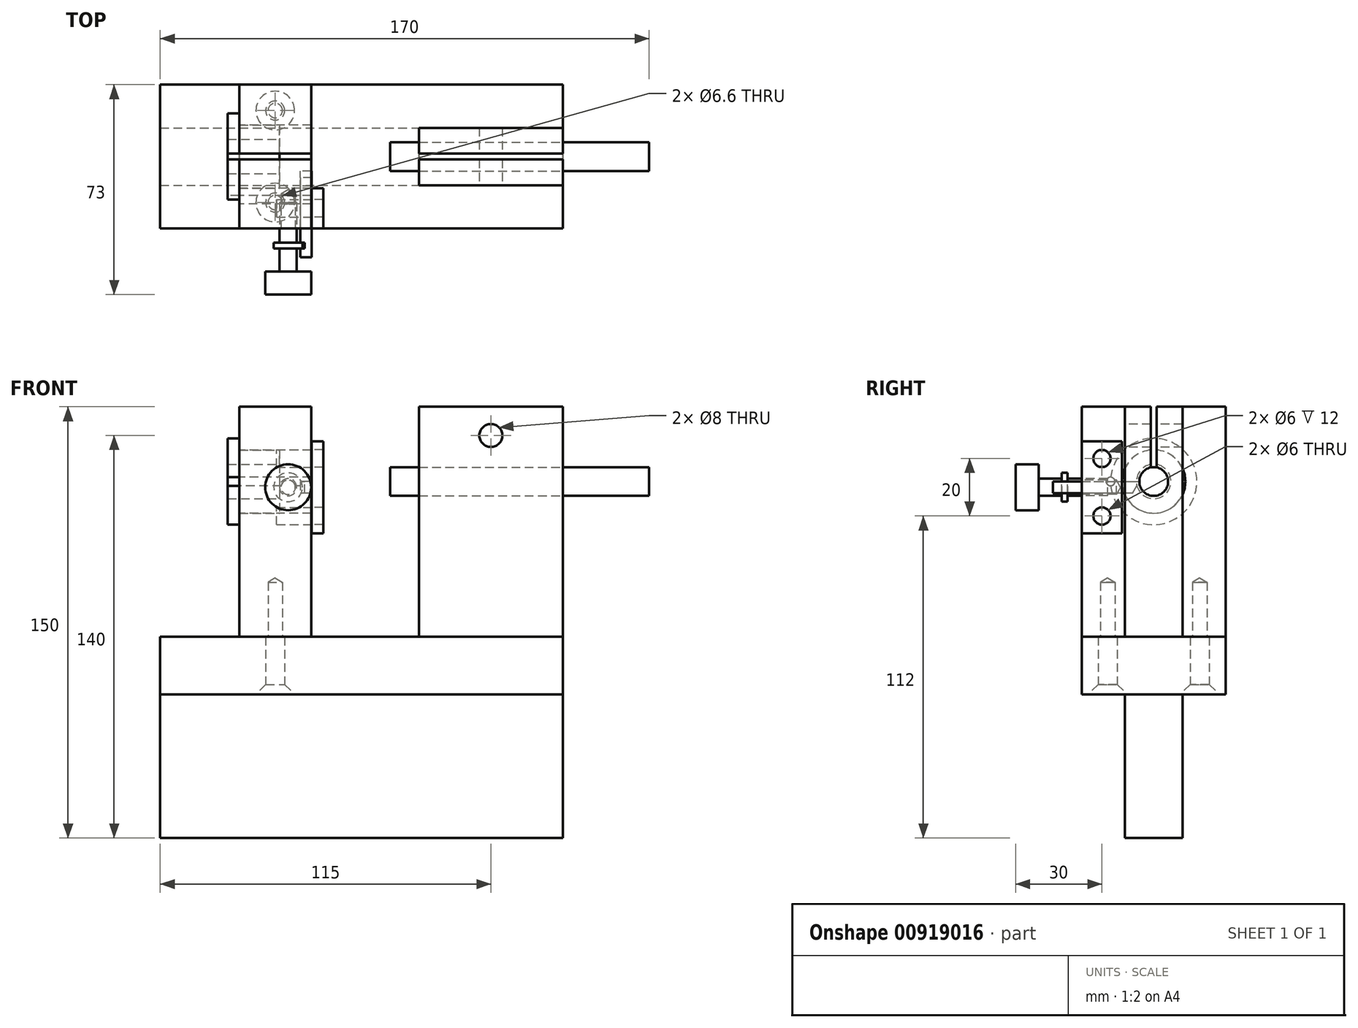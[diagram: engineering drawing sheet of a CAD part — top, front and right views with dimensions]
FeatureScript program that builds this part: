
annotation { "Feature Type Name" : "Feature", "Feature Type Description" : "" }
export const myFeature = defineFeature(function(context is Context, id is Id, definition is map)
    precondition{}
    {
        {
            var Q0;
            Q0=qCreatedBy(makeId("Right.planeOp"),FACE);
            var sketch = newSketch(context, id + "F0", { "sketchPlane" : qUnion([Q0])});
            skCircle(sketch, "E0", {"center": v(0, 0) * mm, "radius": 11 * mm});
            skLineSegment(sketch, "E1.bottom", {"start": v(25, 26) * mm, "end": v(-25, 26) * mm});
            skLineSegment(sketch, "E1.top", {"start": v(25, -54) * mm, "end": v(-25, -54) * mm});
            skLineSegment(sketch, "E1.left", {"start": v(25, 26) * mm, "end": v(25, -54) * mm});
            skLineSegment(sketch, "E1.right", {"start": v(-25, 26) * mm, "end": v(-25, -54) * mm});
            skSolve(sketch);
        }
        {
            var Q0;
            Q0 = qSketchRegion(id + "F0", true);
            extrude(context, id + "F1", {"entities" : qUnion([Q0]), "depth" : 12.5 * mm, "offsetDistance" : 25 * mm, "hasSecondDirection" : true, "secondDirectionOppositeDirection" : true, "secondDirectionDepth" : 12.5 * mm});
        }
        {
            var Q0;
            Q0=makeQuery(id+"F1.opExtrude","CAP_FACE",FACE,{"disambiguationData":[OSD([sQuery(id+"F0.wireOp",EDGE,"E0"),sQuery(id+"F0.wireOp",EDGE,"E1.bottom"),sQuery(id+"F0.wireOp",EDGE,"E1.top"),sQuery(id+"F0.wireOp",EDGE,"E1.left"),sQuery(id+"F0.wireOp",EDGE,"E1.right")])],"isStart":true});
            var sketch = newSketch(context, id + "F2", { "sketchPlane" : qUnion([Q0])});
            skCircle(sketch, "E2", {"center": v(15, 0) * mm, "radius": 1.5 * mm});
            skSolve(sketch);
        }
        {
            var Q0;
            Q0 = qSketchRegion(id + "F2", true);
            extrude(context, id + "F3", {"entities" : qUnion([Q0]), "operationType" : NewBodyOperationType.REMOVE, "oppositeDirection" : true, "depth" : 10 * mm, "offsetDistance" : 25 * mm});
        }
        {
            var Q0;
            Q0=makeQuery(id+"F1.opExtrude","SWEPT_FACE",FACE,{"disambiguationData":[OSD([sQuery(id+"F0.wireOp",EDGE,"E1.top")])]});
            var sketch = newSketch(context, id + "F4", { "sketchPlane" : qUnion([Q0])});
            skLineSegment(sketch, "E3.bottom", {"start": v(100, -25) * mm, "end": v(-40, -25) * mm});
            skLineSegment(sketch, "E3.top", {"start": v(100, 25) * mm, "end": v(-40, 25) * mm});
            skLineSegment(sketch, "E3.left", {"start": v(100, -25) * mm, "end": v(100, 25) * mm});
            skLineSegment(sketch, "E3.right", {"start": v(-40, -25) * mm, "end": v(-40, 25) * mm});
            skPoint(sketch, "E3.middle", {"position": v(0, 0) * mm});
            skSolve(sketch);
        }
        {
            var Q0;
            Q0 = qSketchRegion(id + "F4", true);
            extrude(context, id + "F5", {"entities" : qUnion([Q0]), "depth" : 20 * mm, "offsetDistance" : 25 * mm});
        }
        {
            var Q0;
            Q0=makeQuery(id+"F1.opExtrude","CAP_FACE",FACE,{"disambiguationData":[OSD([sQuery(id+"F0.wireOp",EDGE,"E0"),sQuery(id+"F0.wireOp",EDGE,"E1.bottom"),sQuery(id+"F0.wireOp",EDGE,"E1.top"),sQuery(id+"F0.wireOp",EDGE,"E1.left"),sQuery(id+"F0.wireOp",EDGE,"E1.right")])],"isStart":false});
            var sketch = newSketch(context, id + "F6", { "sketchPlane" : qUnion([Q0])});
            skLineSegment(sketch, "E4.bottom", {"start": v(6, 6) * mm, "end": v(-6, 6) * mm});
            skLineSegment(sketch, "E4.top", {"start": v(6, -6) * mm, "end": v(-6, -6) * mm});
            skLineSegment(sketch, "E4.left", {"start": v(6, 6) * mm, "end": v(6, -6) * mm});
            skLineSegment(sketch, "E4.right", {"start": v(-6, 6) * mm, "end": v(-6, -6) * mm});
            skPoint(sketch, "E4.middle", {"position": v(0, 0) * mm});
            skCircle(sketch, "E5", {"center": v(0, 0) * mm, "radius": 8.49 * mm});
            skCircle(sketch, "E6", {"center": v(0, 0) * mm, "radius": 6 * mm});
            skSolve(sketch);
        }
        {
            var Q0;
            Q0=qCreatedBy(makeId("Front.planeOp"),FACE);
            var sketch = newSketch(context, id + "F7", { "sketchPlane" : qUnion([Q0])});
            skLineSegment(sketch, "E7", {"start": v(16.61, 0) * mm, "end": v(-49.8, 0) * mm, "construction": true});
            skLineSegment(sketch, "E8", {"start": v(1.5, 6) * mm, "end": v(1.5, 11) * mm});
            skLineSegment(sketch, "E9", {"start": v(1.5, 11) * mm, "end": v(-12.5, 11) * mm});
            skLineSegment(sketch, "E10", {"start": v(-12.5, 11) * mm, "end": v(-12.5, 15) * mm});
            skLineSegment(sketch, "E11", {"start": v(-12.5, 15) * mm, "end": v(-16.5, 15) * mm});
            skLineSegment(sketch, "E12", {"start": v(-16.5, 15) * mm, "end": v(-16.5, 6) * mm});
            skLineSegment(sketch, "E13", {"start": v(-16.5, 6) * mm, "end": v(1.5, 6) * mm});
            skSolve(sketch);
        }
        {
            var Q0;
            Q0 = qSketchRegion(id + "F7", true);
            var Q1;
            Q1=sQuery(id+"F7.wireOp",EDGE,"E7");
            revolve(context, id + "F8", {"surfaceOperationType" : NewSurfaceOperationType.NEW, "entities" : qUnion([Q0]), "axis" : qUnion([Q1]), "revolveType" : RevolveType.FULL});
        }
        {
            var Q0;
            Q0=makeQuery(id+"F8.opRevolve","SWEPT_FACE",FACE,{"disambiguationData":[OSD([sQuery(id+"F7.wireOp",EDGE,"E12")])]});
            var sketch = newSketch(context, id + "F9", { "sketchPlane" : qUnion([Q0])});
            skCircle(sketch, "E14", {"center": v(15, 0) * mm, "radius": 1.5 * mm});
            skSolve(sketch);
        }
        {
            var Q0;
            Q0 = qSketchRegion(id + "F9", true);
            extrude(context, id + "F10", {"entities" : qUnion([Q0]), "operationType" : NewBodyOperationType.REMOVE, "endBound" : BoundingType.THROUGH_ALL, "oppositeDirection" : true, "depth" : 25 * mm, "offsetDistance" : 25 * mm});
        }
        {
            var Q0;
            Q0=makeQuery(id+"F6.imprint","IMPRINT",FACE,{"disambiguationData":[TD([[makeQuery(id+"F6.imprint","IMPRINT",EDGE,{"derivedFrom":makeQuery(id+"F1.opExtrude","CAP_EDGE",EDGE,{"disambiguationData":[OSD([sQuery(id+"F0.wireOp",EDGE,"E0")])],"isStart":false})}),-1.0]])]});
            var sketch = newSketch(context, id + "F11", { "sketchPlane" : qUnion([Q0])});
            skLineSegment(sketch, "E15", {"start": v(-36.13, 0) * mm, "end": v(-7.22, 0) * mm});
            skLineSegment(sketch, "E16", {"start": v(-7.22, 0) * mm, "end": v(-10, -4) * mm});
            skLineSegment(sketch, "E17", {"start": v(-10, -4) * mm, "end": v(-36.13, -4) * mm});
            skLineSegment(sketch, "E18", {"start": v(-36.13, -4) * mm, "end": v(-36.13, 0) * mm});
            skSolve(sketch);
        }
        {
            var Q0;
            Q0 = qSketchRegion(id + "F11", true);
            extrude(context, id + "F12", {"entities" : qUnion([Q0]), "operationType" : NewBodyOperationType.REMOVE, "oppositeDirection" : true, "depth" : 3.8 * mm, "offsetDistance" : 25 * mm});
        }
        {
            var Q0;
            Q0=makeQuery(id+"F12.boolean.opBoolean","COPY",FACE,{"derivedFrom":makeQuery(id+"F12.opExtrude","CAP_FACE",FACE,{"disambiguationData":[OSD([sQuery(id+"F11.wireOp",EDGE,"E15"),sQuery(id+"F11.wireOp",EDGE,"E16"),sQuery(id+"F11.wireOp",EDGE,"E17"),sQuery(id+"F11.wireOp",EDGE,"E18")])],"isStart":false})});
            var sketch = newSketch(context, id + "F13", { "sketchPlane" : qUnion([Q0])});
            skLineSegment(sketch, "E19.0", {"start": v(-35, 0) * mm, "end": v(-5, 0) * mm});
            skLineSegment(sketch, "E20.0", {"start": v(-7.3, -4) * mm, "end": v(-35, -4) * mm});
            skLineSegment(sketch, "E21", {"start": v(-7.3, -4) * mm, "end": v(-5, 0) * mm});
            skLineSegment(sketch, "E22", {"start": v(0, 0) * mm, "end": v(0, 13.61) * mm, "construction": true});
            skLineSegment(sketch, "E23", {"start": v(-35, 0) * mm, "end": v(-35, -4) * mm});
            skPoint(sketch, "E24.orphan", {"position": v(-25, 0) * mm});
            skPoint(sketch, "E25.orphan", {"position": v(-25, -4) * mm});
            skPoint(sketch, "E26.orphan", {"position": v(-11, 0) * mm});
            skPoint(sketch, "E27.orphan", {"position": v(-10.25, -4) * mm});
            skSolve(sketch);
        }
        {
            var Q0;
            Q0 = qSketchRegion(id + "F13", true);
            extrude(context, id + "F14", {"entities" : qUnion([Q0]), "depth" : 4 * mm, "offsetDistance" : 25 * mm});
        }
        {
            var Q0;
            Q0=makeQuery(id+"F6.imprint","IMPRINT",FACE,{"disambiguationData":[TD([[makeQuery(id+"F6.imprint","IMPRINT",EDGE,{"derivedFrom":makeQuery(id+"F1.opExtrude","CAP_EDGE",EDGE,{"disambiguationData":[OSD([sQuery(id+"F0.wireOp",EDGE,"E0")])],"isStart":false})}),-1.0]])]});
            var sketch = newSketch(context, id + "F15", { "sketchPlane" : qUnion([Q0])});
            skCircle(sketch, "E28", {"center": v(-18, 8) * mm, "radius": 3 * mm});
            skCircle(sketch, "E29", {"center": v(-18, -12) * mm, "radius": 3 * mm});
            skSolve(sketch);
        }
        {
            var Q0;
            Q0 = qSketchRegion(id + "F15", true);
            extrude(context, id + "F16", {"entities" : qUnion([Q0]), "operationType" : NewBodyOperationType.REMOVE, "oppositeDirection" : true, "depth" : 12 * mm, "offsetDistance" : 25 * mm});
        }
        {
            var Q0;
            Q0=makeQuery(id+"F14.opExtrude","SWEPT_FACE",FACE,{"disambiguationData":[OSD([sQuery(id+"F13.wireOp",EDGE,"E19.0")])]});
            var sketch = newSketch(context, id + "F17", { "sketchPlane" : qUnion([Q0])});
            skLineSegment(sketch, "E30.bottom", {"start": v(8.7, -32) * mm, "end": v(10.2, -32) * mm});
            skLineSegment(sketch, "E30.top", {"start": v(8.7, -30) * mm, "end": v(10.2, -30) * mm});
            skLineSegment(sketch, "E30.left", {"start": v(8.7, -32) * mm, "end": v(8.7, -30) * mm});
            skLineSegment(sketch, "E30.right", {"start": v(10.2, -32) * mm, "end": v(10.2, -30) * mm});
            skSolve(sketch);
        }
        {
            var Q0;
            Q0 = qSketchRegion(id + "F17", true);
            extrude(context, id + "F18", {"entities" : qUnion([Q0]), "operationType" : NewBodyOperationType.REMOVE, "endBound" : BoundingType.THROUGH_ALL, "oppositeDirection" : true, "depth" : 25 * mm, "offsetDistance" : 25 * mm});
        }
        {
            var Q0;
            Q0=makeQuery(id+"F5.opExtrude","CAP_FACE",FACE,{"disambiguationData":[OSD([sQuery(id+"F4.wireOp",EDGE,"E3.bottom"),sQuery(id+"F4.wireOp",EDGE,"E3.top"),sQuery(id+"F4.wireOp",EDGE,"E3.left"),sQuery(id+"F4.wireOp",EDGE,"E3.right")])],"isStart":true});
            var sketch = newSketch(context, id + "F19", { "sketchPlane" : qUnion([Q0])});
            skLineSegment(sketch, "E31.bottom", {"start": v(100, -10) * mm, "end": v(50, -10) * mm});
            skLineSegment(sketch, "E31.top", {"start": v(100, 10) * mm, "end": v(50, 10) * mm});
            skLineSegment(sketch, "E31.left", {"start": v(100, -10) * mm, "end": v(100, 10) * mm});
            skLineSegment(sketch, "E31.right", {"start": v(50, -10) * mm, "end": v(50, 10) * mm});
            skSolve(sketch);
        }
        {
            var Q0;
            Q0 = qSketchRegion(id + "F19", true);
            extrude(context, id + "F20", {"entities" : qUnion([Q0]), "depth" : 80 * mm, "offsetDistance" : 25 * mm});
        }
        {
            var Q0;
            Q0=makeQuery(id+"F20.opExtrude","SWEPT_FACE",FACE,{"disambiguationData":[OSD([sQuery(id+"F19.wireOp",EDGE,"E31.left")])]});
            var sketch = newSketch(context, id + "F21", { "sketchPlane" : qUnion([Q0])});
            skCircle(sketch, "E32", {"center": v(0, 0) * mm, "radius": 5 * mm});
            skSolve(sketch);
        }
        {
            var Q0;
            Q0 = qSketchRegion(id + "F21", true);
            extrude(context, id + "F22", {"entities" : qUnion([Q0]), "operationType" : NewBodyOperationType.REMOVE, "endBound" : BoundingType.THROUGH_ALL, "oppositeDirection" : true, "depth" : 25 * mm, "offsetDistance" : 25 * mm});
        }
        {
            var Q0;
            Q0=makeQuery(id+"F20.opExtrude","SWEPT_FACE",FACE,{"disambiguationData":[OSD([sQuery(id+"F19.wireOp",EDGE,"E31.left")])]});
            var sketch = newSketch(context, id + "F23", { "sketchPlane" : qUnion([Q0])});
            skLineSegment(sketch, "E33.bottom", {"start": v(-1, 0) * mm, "end": v(1, 0) * mm});
            skLineSegment(sketch, "E33.top", {"start": v(-1, 26) * mm, "end": v(1, 26) * mm});
            skLineSegment(sketch, "E33.left", {"start": v(-1, 0) * mm, "end": v(-1, 26) * mm});
            skLineSegment(sketch, "E33.right", {"start": v(1, 0) * mm, "end": v(1, 26) * mm});
            skSolve(sketch);
        }
        {
            var Q0;
            Q0 = qSketchRegion(id + "F23", true);
            extrude(context, id + "F24", {"entities" : qUnion([Q0]), "operationType" : NewBodyOperationType.REMOVE, "endBound" : BoundingType.THROUGH_ALL, "oppositeDirection" : true, "depth" : 25 * mm, "offsetDistance" : 25 * mm});
        }
        {
            var Q0;
            Q0=makeQuery(id+"F20.opExtrude","SWEPT_FACE",FACE,{"disambiguationData":[OSD([sQuery(id+"F19.wireOp",EDGE,"E31.bottom")])]});
            var sketch = newSketch(context, id + "F25", { "sketchPlane" : qUnion([Q0])});
            skCircle(sketch, "E34", {"center": v(75, 16) * mm, "radius": 4 * mm});
            skPoint(sketch, "E34.centerSnap0", {"position": v(75, 26) * mm});
            skSolve(sketch);
        }
        {
            var Q0;
            Q0 = qSketchRegion(id + "F25", true);
            extrude(context, id + "F26", {"entities" : qUnion([Q0]), "operationType" : NewBodyOperationType.REMOVE, "endBound" : BoundingType.THROUGH_ALL, "oppositeDirection" : true, "depth" : 25 * mm, "offsetDistance" : 25 * mm});
        }
        {
            var Q0;
            Q0=makeQuery(id+"F20.opExtrude","SWEPT_FACE",FACE,{"disambiguationData":[OSD([sQuery(id+"F19.wireOp",EDGE,"E31.right")])]});
            var sketch = newSketch(context, id + "F27", { "sketchPlane" : qUnion([Q0])});
            skCircle(sketch, "E35", {"center": v(0, 0) * mm, "radius": 5 * mm});
            skSolve(sketch);
        }
        {
            var Q0;
            Q0 = qSketchRegion(id + "F27", true);
            extrude(context, id + "F28", {"entities" : qUnion([Q0]), "depth" : 10 * mm, "offsetDistance" : 25 * mm, "hasSecondDirection" : true, "secondDirectionOppositeDirection" : true, "secondDirectionDepth" : 80 * mm});
        }
        {
            var Q0;
            Q0=makeQuery(id+"F5.opExtrude","CAP_FACE",FACE,{"disambiguationData":[OSD([sQuery(id+"F4.wireOp",EDGE,"E3.bottom"),sQuery(id+"F4.wireOp",EDGE,"E3.top"),sQuery(id+"F4.wireOp",EDGE,"E3.left"),sQuery(id+"F4.wireOp",EDGE,"E3.right")])],"isStart":false});
            var sketch = newSketch(context, id + "F29", { "sketchPlane" : qUnion([Q0])});
            skPoint(sketch, "E36", {"position": v(0, 16) * mm});
            skPoint(sketch, "E37", {"position": v(0, -16) * mm});
            skSolve(sketch);
        }
        {
            var Q0;
            Q0=sQuery(id+"F29.wireOp",VERTEX,"E37");
            var Q1;
            Q1=sQuery(id+"F29.wireOp",VERTEX,"E36");
            var Q2;
            Q2=makeQuery(id+"F1.opExtrude","SWEPT_BODY",BODY,{"disambiguationData":[OSD([sQuery(id+"F0.wireOp",EDGE,"E0"),sQuery(id+"F0.wireOp",EDGE,"E1.bottom"),sQuery(id+"F0.wireOp",EDGE,"E1.top"),sQuery(id+"F0.wireOp",EDGE,"E1.left"),sQuery(id+"F0.wireOp",EDGE,"E1.right")])]});
            var Q3;
            Q3=makeQuery(id+"F5.opExtrude","SWEPT_BODY",BODY,{"disambiguationData":[OSD([sQuery(id+"F4.wireOp",EDGE,"E3.bottom"),sQuery(id+"F4.wireOp",EDGE,"E3.top"),sQuery(id+"F4.wireOp",EDGE,"E3.left"),sQuery(id+"F4.wireOp",EDGE,"E3.right")])]});
            hole(context, id + "F30", {"style" : HoleStyle.C_SINK, "endStyle" : HoleEndStyle.BLIND_IN_LAST, "standardTappedOrClearance" : lookupTablePath({ "fit" : "Normal", "standard" : "ISO", "size" : "M6", "type" : "Clearance" }), "standardBlindInLast" : lookupTablePath({ "fit" : "Normal", "standard" : "ISO", "engagement" : "75%", "pitch" : "1 mm", "size" : "M6", "type" : "Clearance & tapped" }), "holeDiameter" : 6.6 * mm, "cSinkDiameter" : 13.44 * mm, "cSinkAngle" : 90 * degree, "tapDrillDiameter" : 5 * mm, "majorDiameter" : 6 * mm, "showTappedDepth" : true, "holeDepth" : 19 * mm, "isTappedThrough" : true, "tappedDepth" : 16 * mm, "tapClearance" : 3, "locations" : qUnion([Q0, Q1]), "scope" : qUnion([Q2, Q3])});
        }
        {
            var Q0;
            Q0=makeQuery(id+"F1.opExtrude","SWEPT_FACE",FACE,{"disambiguationData":[OSD([sQuery(id+"F0.wireOp",EDGE,"E1.right")])]});
            var sketch = newSketch(context, id + "F31", { "sketchPlane" : qUnion([Q0])});
            skPoint(sketch, "E38", {"position": v(4.5, -2) * mm});
            skPoint(sketch, "E38.positionSnap0", {"position": v(8.7, -2) * mm});
            skSolve(sketch);
        }
        {
            var Q0;
            Q0=sQuery(id+"F31.wireOp",VERTEX,"E38");
            var Q1;
            Q1=makeQuery(id+"F1.opExtrude","SWEPT_BODY",BODY,{"disambiguationData":[OSD([sQuery(id+"F0.wireOp",EDGE,"E0"),sQuery(id+"F0.wireOp",EDGE,"E1.bottom"),sQuery(id+"F0.wireOp",EDGE,"E1.top"),sQuery(id+"F0.wireOp",EDGE,"E1.left"),sQuery(id+"F0.wireOp",EDGE,"E1.right")])]});
            hole(context, id + "F32", {"style" : HoleStyle.SIMPLE, "endStyle" : HoleEndStyle.BLIND, "standardTappedOrClearance" : lookupTablePath({ "standard" : "ISO", "engagement" : "75%", "pitch" : "1 mm", "size" : "M6", "type" : "Tapped" }), "standardBlindInLast" : lookupTablePath({ "standard" : "ISO", "fit" : "Normal", "engagement" : "75%", "pitch" : "1 mm", "size" : "M6", "type" : "Clearance & tapped" }), "holeDiameter" : 5 * mm, "majorDiameter" : 6 * mm, "showTappedDepth" : true, "holeDepth" : 12 * mm, "isTappedThrough" : true, "tappedDepth" : 9 * mm, "tapClearance" : 3, "locations" : qUnion([Q0]), "scope" : qUnion([Q1])});
        }
        {
            var Q0;
            Q0=makeQuery(id+"F14.opExtrude","CAP_FACE",FACE,{"disambiguationData":[OSD([sQuery(id+"F13.wireOp",EDGE,"E19.0"),sQuery(id+"F13.wireOp",EDGE,"E20.0"),sQuery(id+"F13.wireOp",EDGE,"E21"),sQuery(id+"F13.wireOp",EDGE,"E23")])],"isStart":false});
            var sketch = newSketch(context, id + "F33", { "sketchPlane" : qUnion([Q0])});
            skLineSegment(sketch, "E39.bottom", {"start": v(-25, -18) * mm, "end": v(-11, -18) * mm});
            skLineSegment(sketch, "E39.top", {"start": v(-25, 14) * mm, "end": v(-11, 14) * mm});
            skLineSegment(sketch, "E39.left", {"start": v(-25, -18) * mm, "end": v(-25, 14) * mm});
            skLineSegment(sketch, "E39.right", {"start": v(-11, -18) * mm, "end": v(-11, 14) * mm});
            skCircle(sketch, "E40.0", {"center": v(-18, 8) * mm, "radius": 3 * mm});
            skCircle(sketch, "E41.0", {"center": v(-18, -12) * mm, "radius": 3 * mm});
            skSolve(sketch);
        }
        {
            var Q0;
            Q0 = qSketchRegion(id + "F33", true);
            extrude(context, id + "F34", {"entities" : qUnion([Q0]), "depth" : 4 * mm, "offsetDistance" : 25 * mm});
        }
        {
            var Q0;
            Q0=makeQuery(id+"F1.opExtrude","SWEPT_FACE",FACE,{"disambiguationData":[OSD([sQuery(id+"F0.wireOp",EDGE,"E1.right")])]});
            var sketch = newSketch(context, id + "F35", { "sketchPlane" : qUnion([Q0])});
            skPoint(sketch, "E42", {"position": v(4.5, -2) * mm});
            skSolve(sketch);
        }
        {
            var Q0;
            Q0=qCreatedBy(makeId("Right.planeOp"),FACE);
            var Q1;
            Q1=sQuery(id+"F35.wireOp",VERTEX,"E42");
            cPlane(context, id + "F36", {"entities" : qUnion([Q0, Q1]), "cplaneType" : CPlaneType.PLANE_POINT, "offset" : 25 * mm, "width" : 150 * mm, "height" : 150 * mm});
        }
        {
            var Q0;
            Q0=qCreatedBy(id+"F36.planeOp",FACE);
            var sketch = newSketch(context, id + "F37", { "sketchPlane" : qUnion([Q0])});
            skLineSegment(sketch, "E43", {"start": v(-11.5, -2) * mm, "end": v(-46.13, -2) * mm, "construction": true});
            skLineSegment(sketch, "E44", {"start": v(-16, -2) * mm, "end": v(-16, 1) * mm});
            skLineSegment(sketch, "E45", {"start": v(-16, 1) * mm, "end": v(-30, 1) * mm});
            skLineSegment(sketch, "E46", {"start": v(-30, 1) * mm, "end": v(-30, 3) * mm});
            skLineSegment(sketch, "E47", {"start": v(-30, 3) * mm, "end": v(-32, 3) * mm});
            skLineSegment(sketch, "E48", {"start": v(-32, 3) * mm, "end": v(-32, 1) * mm});
            skLineSegment(sketch, "E49", {"start": v(-32, 1) * mm, "end": v(-40, 1) * mm});
            skLineSegment(sketch, "E50", {"start": v(-40, 1) * mm, "end": v(-40, 6) * mm});
            skLineSegment(sketch, "E51", {"start": v(-40, 6) * mm, "end": v(-48, 6) * mm});
            skLineSegment(sketch, "E52", {"start": v(-48, 6) * mm, "end": v(-48, -2) * mm});
            skLineSegment(sketch, "E53", {"start": v(-48, -2) * mm, "end": v(-16, -2) * mm});
            skSolve(sketch);
        }
        {
            var Q0;
            Q0 = qSketchRegion(id + "F37", true);
            var Q1;
            Q1=sQuery(id+"F37.wireOp",EDGE,"E53");
            revolve(context, id + "F38", {"surfaceOperationType" : NewSurfaceOperationType.NEW, "entities" : qUnion([Q0]), "axis" : qUnion([Q1]), "revolveType" : RevolveType.FULL});
        }
        {
            var Q0;
            Q0=makeQuery(id+"F5.opExtrude","CAP_FACE",FACE,{"disambiguationData":[OSD([sQuery(id+"F4.wireOp",EDGE,"E3.bottom"),sQuery(id+"F4.wireOp",EDGE,"E3.top"),sQuery(id+"F4.wireOp",EDGE,"E3.left"),sQuery(id+"F4.wireOp",EDGE,"E3.right")])],"isStart":false});
            var sketch = newSketch(context, id + "F39", { "sketchPlane" : qUnion([Q0])});
            skLineSegment(sketch, "E54.bottom", {"start": v(-40, 10) * mm, "end": v(100, 10) * mm});
            skLineSegment(sketch, "E54.top", {"start": v(-40, -10) * mm, "end": v(100, -10) * mm});
            skLineSegment(sketch, "E54.left", {"start": v(-40, 10) * mm, "end": v(-40, -10) * mm});
            skLineSegment(sketch, "E54.right", {"start": v(100, 10) * mm, "end": v(100, -10) * mm});
            skSolve(sketch);
        }
        {
            var Q0;
            Q0 = qSketchRegion(id + "F39", true);
            extrude(context, id + "F40", {"entities" : qUnion([Q0]), "depth" : 50 * mm, "offsetDistance" : 25 * mm});
        }
    });
